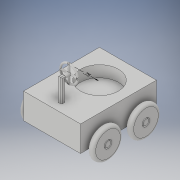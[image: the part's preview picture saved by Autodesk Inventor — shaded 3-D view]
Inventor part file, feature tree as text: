
AUTODESK INVENTOR PART (.ipt)
format: ipt  version: 2018 (Build 220112000, 112)  size: 443,904 bytes
history: native  units: in
note: dims shown in document units (in); Inventor stores cm internally (conversion verified against a paired STEP export)
features: extrude x14, sketch x14, fillet x11, other x2, chamfer x1
ambient origin geometry x8: Origin, YZ Plane, XZ Plane, XY Plane, X Axis, Y Axis, Z Axis, Center Point
bodies: Solid1 (feature_tree)
feature tree (42):
  other  "Annotations"
  extrude  "Extrusion1"  Depth=2.0in
  extrude  "Extrusion2"  Depth=1.25in
  extrude  "Extrusion3"  Depth=0.3in TaperAngle=0.0deg
  extrude  "Extrusion4"  Depth=0.2in
  extrude  "Extrusion5"  Depth=0.15in TaperAngle=0.0deg
  extrude  "Extrusion6"  Depth=0.2in
  extrude  "Extrusion7"  Depth=0.15in TaperAngle=0.0deg
  extrude  "Extrusion8"  Depth=0.15in TaperAngle=0.0deg
  extrude  "Extrusion9"  Depth=0.15in TaperAngle=0.0deg
  extrude  "Extrusion10"  Depth=0.8in
  fillet  "Fillet1"  Radius=0.15in
  fillet  "Fillet2"  Radius=0.2in
  fillet  "Fillet3"  Radius=0.8in
  fillet  "Fillet4"  Radius=0.15in
  extrude  "Extrusion11"  Depth=0.8in
  extrude  "Extrusion12"  Depth=0.15in
  extrude  "Extrusion13"  Depth=0.15in TaperAngle=0.0deg
  fillet  "Fillet5"  Radius=0.075in
  fillet  "Fillet6"  Radius=0.075in
  extrude  "Extrusion14"  Depth=0.075in
  fillet  "Fillet7"  Radius=0.25in
  fillet  "Fillet8"  Radius=0.05in
  fillet  "Fillet9"  Radius=0.05in
  fillet  "Fillet10"  Radius=0.1in
  fillet  "Fillet11"  Radius=0.1in
  chamfer  "Chamfer1"  Distance=0.1in
  sketch  "Sketch1"  dims[d0=1.5in d1=2.0in]
  sketch  "Sketch2"  dims[d2=0.8in d3=0.0in d4=1.25in]
  sketch  "Sketch3"  dims[d5=1.0in d9=0.3in d10=0.0in]
  sketch  "Sketch4"  dims[d11=0.5in d12=0.2in]
  sketch  "Sketch5"  dims[d13=0.15in d14=0.15in d15=0.0in]
  sketch  "Sketch6"  dims[d16=0.5in d17=0.2in]
  sketch  "Sketch7"  dims[d18=0.15in d19=0.15in d20=0.0in]
  sketch  "Sketch8"  dims[d21=0.5in d22=0.15in d23=0.0in]
  sketch  "Sketch9"  dims[d24=0.5in d25=0.15in d26=0.0in]
  sketch  "Sketch10"  dims[d27=0.2in d28=0.8in d29=0.15in d30=0.0in d31=0.2in d32=0.8in d33=0.15in d34=0.0in]
  sketch  "Sketch11"  dims[d35=0.2in d36=0.8in]
  sketch  "Sketch12"  dims[d37=0.15in d38=0.0in d39=0.2in]
  sketch  "Sketch13"  dims[d40=0.8in d41=0.15in d42=0.0in d43=0.075in d44=0.075in]
  sketch  "Sketch14"  dims[d45=0.075in d46=0.075in d47=0.25in d48=0.05in d49=0.05in d50=0.1in d51=0.1in d52=0.1in d53=0.6in d54=0.0in d55=0.05in d56=0.1in d57=0.15in d58=0.0in d59=0.5in d60=0.4in d61=0.05in d62=0.0in d63=0.025in d64=0.025in d65=0.025in d66=0.22in d67=0.05in d68=0.025in d69=0.22in d70=0.05in d71=0.22in d72=0.22in d73=0.05in d74=0.0in d75=0.025in d76=0.025in d77=0.025in d78=0.025in d79=0.025in d80=0.125in d81=0.125in d82=45.0deg d6=0.2069in d7=0.0in d8=0.75in]
  other  "Linear Dimension 1"
